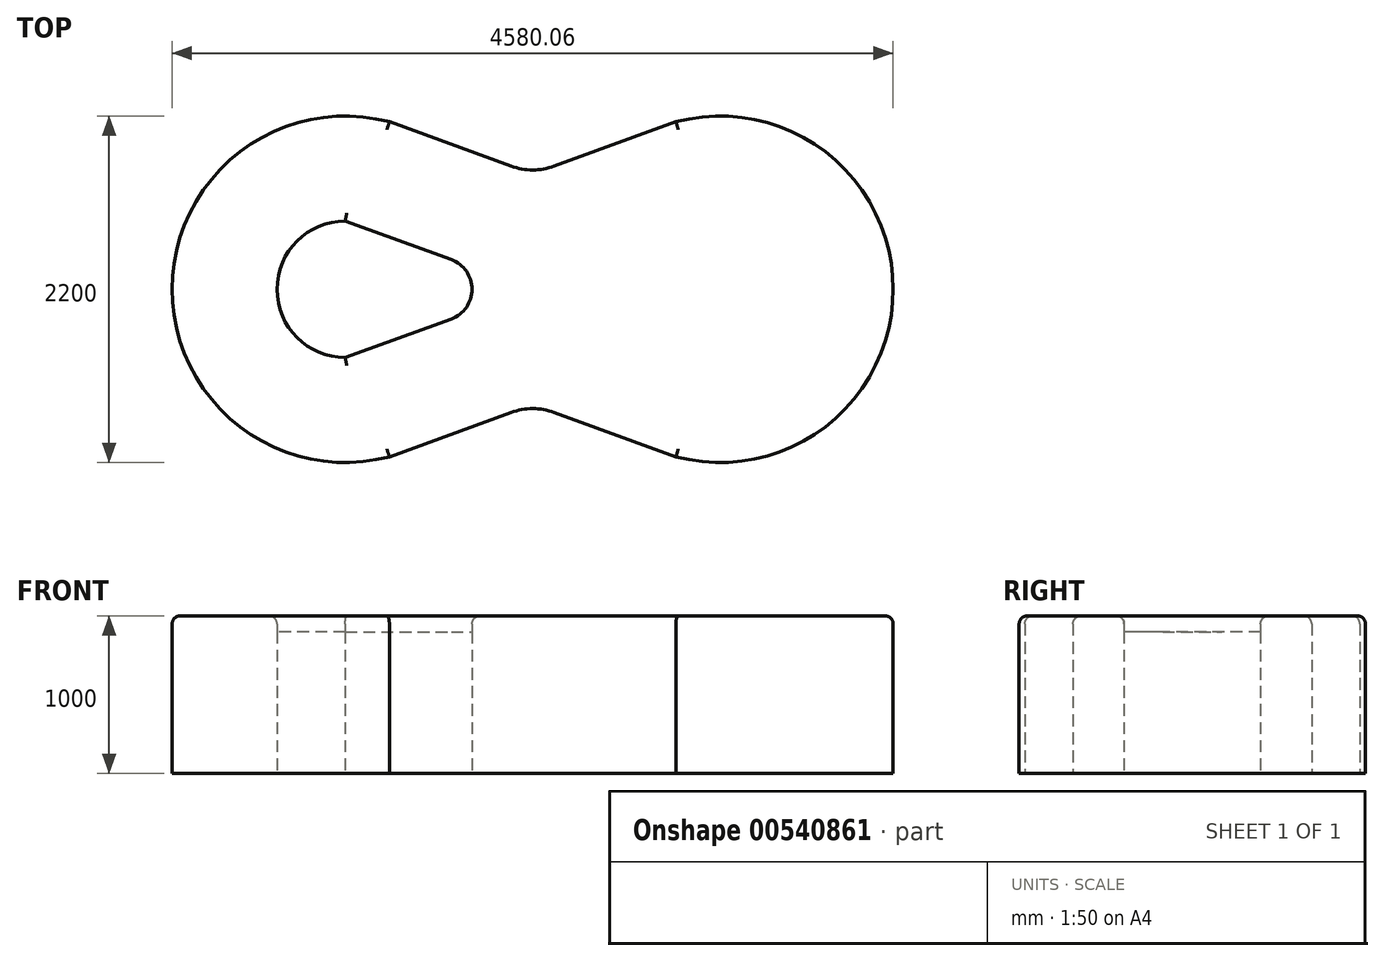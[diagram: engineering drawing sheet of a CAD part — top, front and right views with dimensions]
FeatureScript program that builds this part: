
annotation { "Feature Type Name" : "Feature", "Feature Type Description" : "" }
export const myFeature = defineFeature(function(context is Context, id is Id, definition is map)
    precondition{}
    {
        {
            var Q0;
            Q0=qCreatedBy(makeId("Top.planeOp"),FACE);
            var sketch = newSketch(context, id + "F0", { "sketchPlane" : qUnion([Q0])});
            skArc(sketch, "E0.MirrorCS", {"start": v(-1190.03, -433.13) * mm, "mid": v(-1623.16, 0) * mm, "end": v(-1190.03, 433.13) * mm});
            skLineSegment(sketch, "E1.0", {"start": v(-939.7, 968.16) * mm, "end": v(-171.01, 688.38) * mm});
            skArc(sketch, "E2.0", {"start": v(-939.7, -968.16) * mm, "mid": v(-2190.03, 0) * mm, "end": v(-939.7, 968.16) * mm});
            skLineSegment(sketch, "E3.0", {"start": v(-939.7, -968.16) * mm, "end": v(-171.01, -688.38) * mm});
            skLineSegment(sketch, "E4", {"start": v(-1190.03, 433.13) * mm, "end": v(-516.36, 187.94) * mm});
            skLineSegment(sketch, "E5", {"start": v(-516.36, -187.94) * mm, "end": v(-1190.03, -433.13) * mm});
            skLineSegment(sketch, "E6.MirrorCS", {"start": v(939.7, -968.16) * mm, "end": v(171.01, -688.38) * mm});
            skLineSegment(sketch, "E7.MirrorCS", {"start": v(939.7, 968.16) * mm, "end": v(171.01, 688.38) * mm});
            skArc(sketch, "E8.MirrorCS", {"start": v(1190.03, -433.13) * mm, "mid": v(1623.16, 0) * mm, "end": v(1190.03, 433.13) * mm});
            skArc(sketch, "E9.MirrorCS", {"start": v(939.7, -968.16) * mm, "mid": v(2190.03, 0) * mm, "end": v(939.7, 968.16) * mm});
            skLineSegment(sketch, "E10.MirrorCS", {"start": v(516.36, -187.94) * mm, "end": v(1190.03, -433.13) * mm});
            skLineSegment(sketch, "E11.MirrorCS", {"start": v(1190.03, 433.13) * mm, "end": v(516.36, 187.94) * mm});
            skPoint(sketch, "E12.visualSharp", {"position": v(0, 0) * mm});
            skArc(sketch, "E12.filletArc", {"start": v(-516.36, -187.94) * mm, "mid": v(-384.76, 0) * mm, "end": v(-516.36, 187.94) * mm});
            skArc(sketch, "E13.filletArc", {"start": v(516.36, 187.94) * mm, "mid": v(384.76, 0) * mm, "end": v(516.36, -187.94) * mm});
            skPoint(sketch, "E14.visualSharp", {"position": v(0, 626.14) * mm});
            skArc(sketch, "E14.filletArc", {"start": v(-171.01, 688.38) * mm, "mid": v(0, 658.23) * mm, "end": v(171.01, 688.38) * mm});
            skPoint(sketch, "E15.visualSharp", {"position": v(0, -626.14) * mm});
            skArc(sketch, "E15.filletArc", {"start": v(171.01, -688.38) * mm, "mid": v(0, -658.23) * mm, "end": v(-171.01, -688.38) * mm});
            skLineSegment(sketch, "E16.0", {"start": v(-909.9, -1063.73) * mm, "end": v(-136.8, -782.35) * mm});
            skArc(sketch, "E16.1", {"start": v(136.8, -782.35) * mm, "mid": v(0, -758.23) * mm, "end": v(-136.8, -782.35) * mm});
            skArc(sketch, "E16.2", {"start": v(-909.9, -1063.73) * mm, "mid": v(-2290.03, 0) * mm, "end": v(-909.9, 1063.73) * mm});
            skLineSegment(sketch, "E16.3", {"start": v(909.9, -1063.73) * mm, "end": v(136.8, -782.35) * mm});
            skLineSegment(sketch, "E16.4", {"start": v(-909.9, 1063.73) * mm, "end": v(-136.8, 782.35) * mm});
            skArc(sketch, "E16.5", {"start": v(-136.8, 782.35) * mm, "mid": v(0, 758.23) * mm, "end": v(136.8, 782.35) * mm});
            skLineSegment(sketch, "E16.6", {"start": v(909.9, 1063.73) * mm, "end": v(136.8, 782.35) * mm});
            skArc(sketch, "E16.7", {"start": v(909.9, -1063.73) * mm, "mid": v(2290.03, 0) * mm, "end": v(909.9, 1063.73) * mm});
            skSolve(sketch);
        }
        {
            var Q0;
            Q0=makeQuery(id+"F0.imprint","IMPRINT",FACE,{"disambiguationData":[TD([[makeQuery(id+"F0.imprint","IMPRINT",EDGE,{"derivedFrom":sQuery(id+"F0.wireOp",EDGE,"E1.0")}),1.0]])]});
            var Q1;
            Q1=makeQuery(id+"F0.imprint","IMPRINT",FACE,{"disambiguationData":[TD([[makeQuery(id+"F0.imprint","IMPRINT",EDGE,{"derivedFrom":sQuery(id+"F0.wireOp",EDGE,"E8.MirrorCS")}),1.0]])]});
            var Q2;
            Q2=makeQuery(id+"F0.imprint","IMPRINT",FACE,{"disambiguationData":[TD([[makeQuery(id+"F0.imprint","IMPRINT",EDGE,{"derivedFrom":sQuery(id+"F0.wireOp",EDGE,"E0.MirrorCS")}),-1.0]])]});
            extrude(context, id + "F1", {"entities" : qUnion([Q0, Q1, Q2]), "depth" : 1000 * mm, "offsetDistance" : 25 * mm});
        }
        {
            var Q0;
            Q0=makeQuery(id+"F0.imprint","IMPRINT",FACE,{"disambiguationData":[TD([[makeQuery(id+"F0.imprint","IMPRINT",EDGE,{"derivedFrom":sQuery(id+"F0.wireOp",EDGE,"E0.MirrorCS")}),1.0]])]});
            extrude(context, id + "F2", {"entities" : qUnion([Q0]), "operationType" : NewBodyOperationType.ADD, "depth" : 100 * mm, "offsetDistance" : 25 * mm});
        }
        {
            var Q0;
            Q0=makeQuery(id+"F0.imprint","IMPRINT",FACE,{"disambiguationData":[TD([[makeQuery(id+"F0.imprint","IMPRINT",EDGE,{"derivedFrom":sQuery(id+"F0.wireOp",EDGE,"E0.MirrorCS")}),1.0]])]});
            extrude(context, id + "F3", {"entities" : qUnion([Q0]), "depth" : 900 * mm, "offsetDistance" : 25 * mm});
        }
        {
            var Q0;
            Q0=makeQuery(id+"F1.opExtrude","CAP_FACE",FACE,{"disambiguationData":[OSD([sQuery(id+"F0.wireOp",EDGE,"E1.0"),sQuery(id+"F0.wireOp",EDGE,"E2.0"),sQuery(id+"F0.wireOp",EDGE,"E3.0"),sQuery(id+"F0.wireOp",EDGE,"E6.MirrorCS"),sQuery(id+"F0.wireOp",EDGE,"E7.MirrorCS"),sQuery(id+"F0.wireOp",EDGE,"E9.MirrorCS"),sQuery(id+"F0.wireOp",EDGE,"E14.filletArc"),sQuery(id+"F0.wireOp",EDGE,"E15.filletArc"),sQuery(id+"F0.wireOp",EDGE,"E16.0"),sQuery(id+"F0.wireOp",EDGE,"E16.1"),sQuery(id+"F0.wireOp",EDGE,"E16.2"),sQuery(id+"F0.wireOp",EDGE,"E16.3"),sQuery(id+"F0.wireOp",EDGE,"E16.4"),sQuery(id+"F0.wireOp",EDGE,"E16.5"),sQuery(id+"F0.wireOp",EDGE,"E16.6"),sQuery(id+"F0.wireOp",EDGE,"E16.7")])],"isStart":false});
            var Q1;
            Q1=makeQuery(id+"F1.opExtrude","CAP_FACE",FACE,{"disambiguationData":[OSD([sQuery(id+"F0.wireOp",EDGE,"E0.MirrorCS"),sQuery(id+"F0.wireOp",EDGE,"E4"),sQuery(id+"F0.wireOp",EDGE,"E5"),sQuery(id+"F0.wireOp",EDGE,"E12.filletArc")])],"isStart":false});
            var Q2;
            Q2=makeQuery(id+"F1.opExtrude","CAP_FACE",FACE,{"disambiguationData":[OSD([sQuery(id+"F0.wireOp",EDGE,"E8.MirrorCS"),sQuery(id+"F0.wireOp",EDGE,"E10.MirrorCS"),sQuery(id+"F0.wireOp",EDGE,"E11.MirrorCS"),sQuery(id+"F0.wireOp",EDGE,"E13.filletArc")])],"isStart":false});
            fillet(context, id + "F4", {"entities" : qUnion([Q0, Q1, Q2]), "radius" : 50 * mm, "tangentPropagation" : true, "allowEdgeOverflow" : false});
        }
    });
